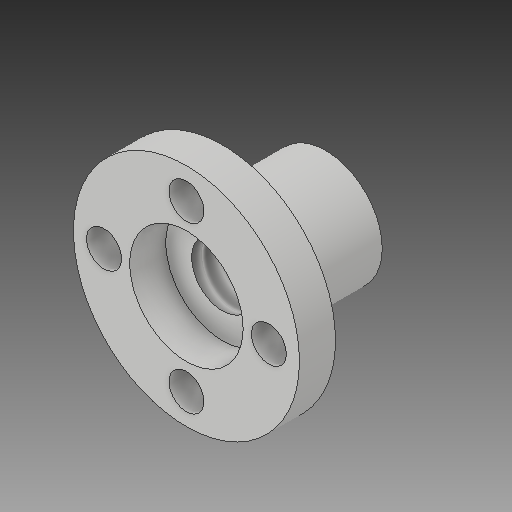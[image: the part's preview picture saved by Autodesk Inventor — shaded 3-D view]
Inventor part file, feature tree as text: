
AUTODESK INVENTOR PART (.ipt)
format: ipt  version: 2018 (Build 220112000, 112)  size: 140,800 bytes
history: native  units: mm
features: other x3, sketch x3
ambient origin geometry x8: Origin, YZ Plane, XZ Plane, XY Plane, X Axis, Y Axis, Z Axis, Center Point
bodies: Solid1 (feature_tree)
feature tree (6):
  other  "Brass-Nut.ipt"
  other  "Solid1::Brass-Nut.ipt"
  other  "TaggingFeature1"
  sketch  "Sketch1"  dims[d0=10.0mm]
  sketch  "Sketch2"
  sketch  "Sketch3"
